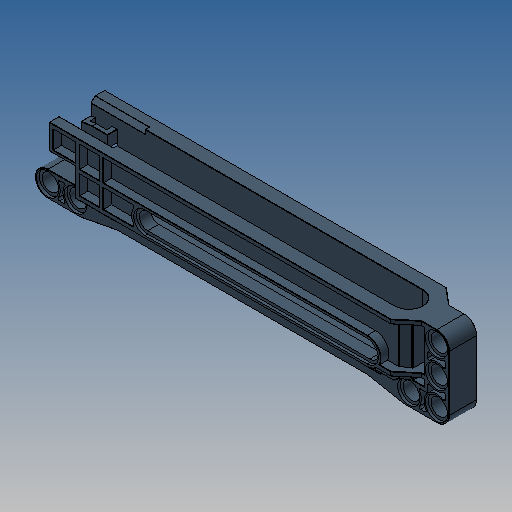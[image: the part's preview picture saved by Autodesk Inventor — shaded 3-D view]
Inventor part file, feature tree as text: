
AUTODESK INVENTOR PART (.ipt)
format: ipt  version: 2025 (Build 290162010, 162A)  size: 1,013,248 bytes
history: native  units: in
note: dims shown in document units (in); Inventor stores cm internally (conversion verified against a paired STEP export)
features: extrude x23, sketch x11, projected_geometry x5, plane x2, pattern_linear x2, mirror x1, fillet x1
ambient origin geometry x8: Origin, YZ Plane, XZ Plane, XY Plane, X Axis, Y Axis, Z Axis, Center Point
bodies: Solid1 (feature_tree)
feature tree (45):
  sketch  "Sketch2"  dims[d0=0.2835in d1=0.315in]
  plane  "Work Plane2"
  extrude  "Extrusion3"  Depth=0.315in
  plane  "Work Plane1"
  extrude  "Extrusion4"  Depth=0.189in
  sketch  "Sketch5"  dims[d6=0.5197in d7=0.9291in]
  extrude  "Extrusion5"  Depth=3.7795in
  extrude  "Extrusion6"  Depth=0.9291in
  sketch  "Sketch6"  dims[d8=0.0787in d9=3.6535in]
  extrude  "Extrusion7"  Depth=3.6535in
  extrude  "Extrusion10"  Depth=0.315in
  extrude  "Extrusion8"  Depth=0.2835in
  extrude  "Extrusion9"  Depth=0.8031in
  extrude  "Extrusion11"  Depth=0.063in
  sketch  "Sketch9"  dims[d15=0.2835in d16=0.8031in]
  extrude  "Extrusion12"  Depth=0.0945in
  extrude  "Extrusion13"  Depth=0.0157in
  extrude  "Extrusion14"  Depth=0.0157in
  extrude  "Extrusion15"  Depth=0.0157in
  extrude  "Extrusion16"  TaperAngle=0.0deg  [1 undecoded]
  sketch  "Sketch8"  dims[d12=0.0472in d13=0.2835in]
  extrude  "Extrusion17"  Depth=0.0157in
  extrude  "Extrusion18"  Depth=0.0157in
  extrude  "Extrusion19"  Depth=0.189in
  extrude  "Extrusion20"  Depth=0.0157in
  extrude  "Extrusion21"  Depth=0.0157in
  pattern_linear  "Rectangular Pattern1"  Spacing1=0.0472in  [1 undecoded]
  pattern_linear  "Rectangular Pattern2"  Spacing1=0.0472in  [1 undecoded]
  mirror  "Mirror1"
  extrude  "Extrusion24"  Depth=0.0157in
  extrude  "Extrusion22"  Depth=0.0157in TaperAngle=0.0deg
  extrude  "Extrusion2"  Depth=0.0157in TaperAngle=0.0deg
  extrude  "Extrusion23"  Depth=0.0157in TaperAngle=0.0deg
  fillet  "Fillet1"  Radius=0.315in
  sketch  "Sketch3"  dims[d2=0.189in d3=0.252in]
  sketch  "Sketch4"  dims[d4=0.315in d5=3.7795in]
  projected_geometry  "Projected Loop1"
  projected_geometry  "Projected Loop2"
  sketch  "Sketch7"  dims[d10=2.8346in d11=0.315in]
  projected_geometry  "Projected Loop3"
  sketch  "Sketch10"  dims[d17=0.126in d18=0.063in]
  projected_geometry  "Projected Loop4"
  projected_geometry  "Projected Loop5"
  sketch  "Sketch11"  dims[d19=0.1575in d20=0.0945in]
  sketch  "Sketch12"  dims[d21=2.8346in d22=0.242in d23=0.1575in d26=0.252in d27=0.0in d28=0.315in d29=0.6299in d30=0.189in d31=0.2992in d32=3.874in d33=0.0472in d34=0.0in d37=0.0472in d38=0.0in d41=0.4409in d43=0.0472in d44=0.0in d46=0.0866in d47=0.0in d49=0.0945in d50=0.0in d51=0.315in d56=0.315in d57=0.0315in d58=0.0945in d59=0.189in d60=0.063in d61=0.252in d62=0.0787in d63=-0.1825in d64=0.315in d65=0.0in d67=0.5118in d69=0.0787in d70=0.0in d71=0.063in d72=0.0472in d73=0.0787in d74=0.0787in d75=0.0in d76=0.0472in d77=0.0472in d80=0.1102in d81=0.0in d82=0.0in d83=0.2992in d84=0.0in d85=0.6142in d86=0.0in d87=0.063in d88=0.189in d89=0.252in d90=0.0in d91=0.0157in d92=0.126in d93=0.252in d94=0.0in d95=0.4449in d96=0.5984in d98=0.2992in d99=0.1575in d100=0.0472in d101=0.0472in d102=0.0472in d103=0.189in d104=0.252in d105=2.5197in d106=0.2677in d108=0.0472in d109=0.2205in d110=0.252in d111=0.0in d112=0.252in d113=0.0in d114=0.252in d115=0.0in d116=0.0315in d117=0.0in d118=0.1575in d119=0.0472in d120=0.0in d121=0.7874in d123=0.2677in d124=0.7874in d126=3.2598in d127=0.0472in d128=0.0in d129=45.0deg d130=0.063in d131=0.0in d136=0.0472in d137=0.2835in d138=0.063in d139=0.0in d140=0.0039in d141=0.0157in]
note: 3 required parameter values undecoded (feature->parameter linkage not recoverable at this tier; creation-order binding heuristic only, values carry confidence <= 0.55)
